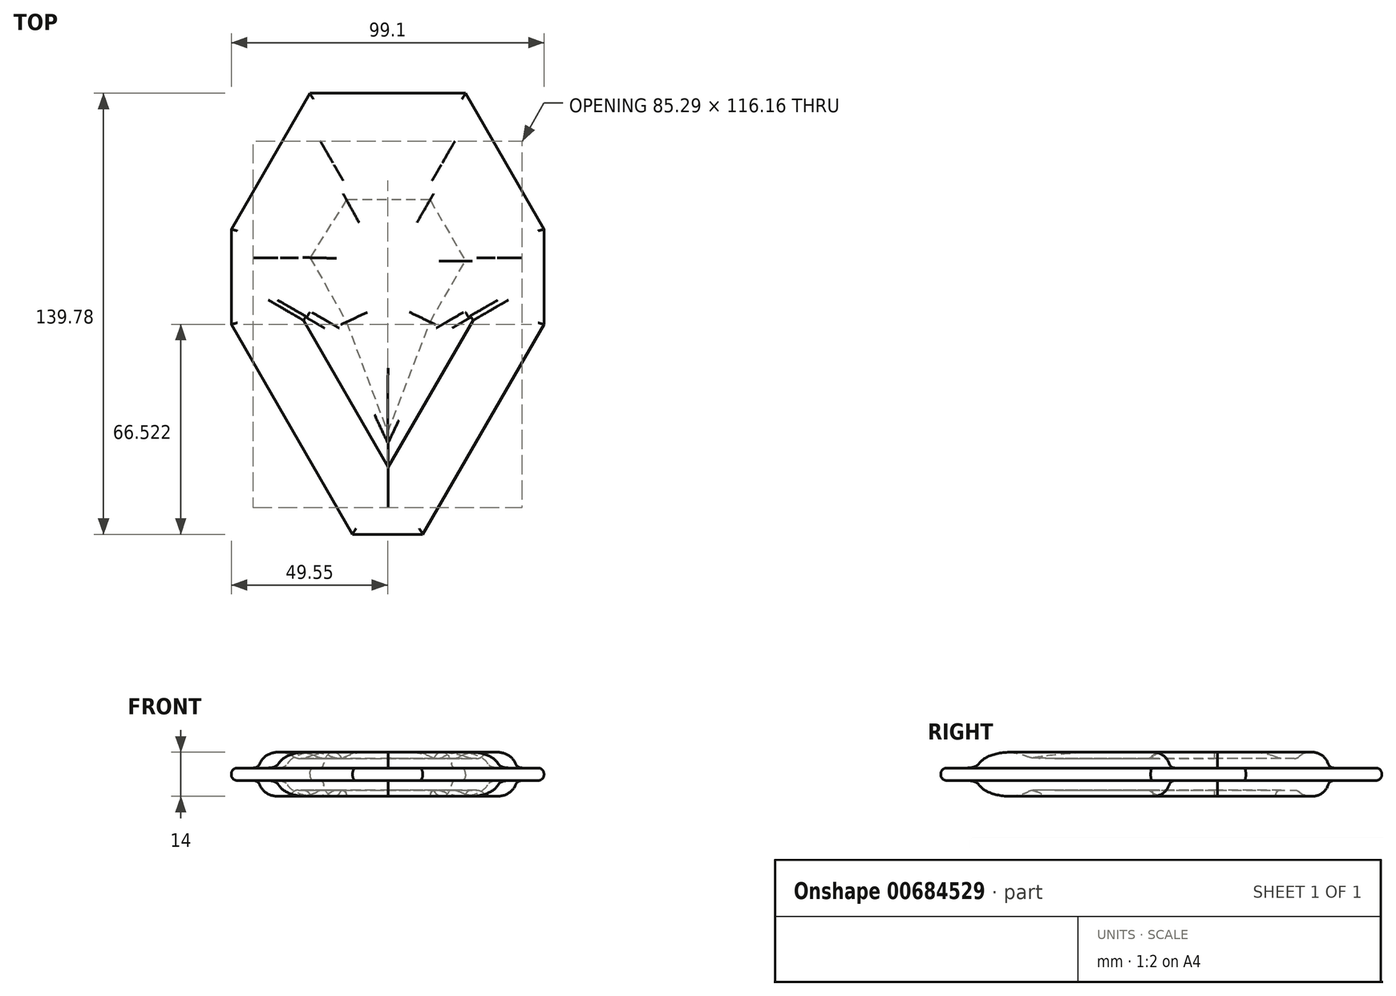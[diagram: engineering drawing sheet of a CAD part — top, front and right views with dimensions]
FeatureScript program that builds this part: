
annotation { "Feature Type Name" : "Feature", "Feature Type Description" : "" }
export const myFeature = defineFeature(function(context is Context, id is Id, definition is map)
    precondition{}
    {
        {
            var Q0;
            Q0=qCreatedBy(makeId("Top.planeOp"),FACE);
            var sketch = newSketch(context, id + "F0", { "sketchPlane" : qUnion([Q0])});
            skCircle(sketch, "E0.cCircle", {"center": v(0, 0) * mm, "radius": 35 * mm, "construction": true});
            skLineSegment(sketch, "E0.0", {"start": v(-20.2, 35) * mm, "end": v(20.2, 35) * mm});
            skLineSegment(sketch, "E0.1", {"start": v(20.2, 35) * mm, "end": v(40.41, 0) * mm});
            skLineSegment(sketch, "E0.2", {"start": v(40.41, 0) * mm, "end": v(31.54, -15.36) * mm});
            skLineSegment(sketch, "E0.4", {"start": v(-31.54, -15.36) * mm, "end": v(-40.41, 0) * mm});
            skLineSegment(sketch, "E0.5", {"start": v(-40.41, 0) * mm, "end": v(-20.2, 35) * mm});
            skPoint(sketch, "E0.0.midPoint", {"position": v(0, 35) * mm});
            skCircle(sketch, "E1.cCircle", {"center": v(0.21, -35.36) * mm, "radius": 20 * mm, "construction": true});
            skLineSegment(sketch, "E1.0", {"start": v(-34.43, -15.36) * mm, "end": v(-31.45, -15.36) * mm});
            skLineSegment(sketch, "E1.1", {"start": v(34.85, -15.36) * mm, "end": v(0.21, -75.36) * mm});
            skLineSegment(sketch, "E1.2", {"start": v(0.21, -75.36) * mm, "end": v(-34.43, -15.36) * mm});
            skPoint(sketch, "E1.0.midPoint", {"position": v(0.21, -15.36) * mm});
            skLineSegment(sketch, "E2.trimOffspring", {"start": v(31.45, -15.36) * mm, "end": v(34.85, -15.36) * mm});
            skPoint(sketch, "E3.orphan", {"position": v(20.2, -35) * mm});
            skPoint(sketch, "E0.3.end.orphan", {"position": v(-19.79, -35.73) * mm});
            skLineSegment(sketch, "E4.0", {"start": v(30.48, 0) * mm, "end": v(18.73, -20.36) * mm});
            skLineSegment(sketch, "E4.1", {"start": v(-18.73, -20.36) * mm, "end": v(-30.48, 0) * mm});
            skLineSegment(sketch, "E4.2", {"start": v(-30.48, 0) * mm, "end": v(-15.24, 26.4) * mm});
            skLineSegment(sketch, "E4.3", {"start": v(-15.24, 26.4) * mm, "end": v(15.24, 26.4) * mm});
            skLineSegment(sketch, "E4.4", {"start": v(15.24, 26.4) * mm, "end": v(30.48, 0) * mm});
            skLineSegment(sketch, "E5.0", {"start": v(0.21, -61.16) * mm, "end": v(-23.35, -20.36) * mm});
            skLineSegment(sketch, "E5.1", {"start": v(23.77, -20.36) * mm, "end": v(0.21, -61.16) * mm});
            skLineSegment(sketch, "E6.0", {"start": v(-23.35, -20.36) * mm, "end": v(-18.73, -20.36) * mm});
            skLineSegment(sketch, "E7.0", {"start": v(18.73, -20.36) * mm, "end": v(23.77, -20.36) * mm});
            skLineSegment(sketch, "E8", {"start": v(-13.02, -20.36) * mm, "end": v(0, -55.36) * mm});
            skLineSegment(sketch, "E9", {"start": v(0, -55.36) * mm, "end": v(13.44, -20.36) * mm});
            skLineSegment(sketch, "E10", {"start": v(13.44, 18.32) * mm, "end": v(-13.02, 18.32) * mm});
            skLineSegment(sketch, "E11", {"start": v(-13.02, 18.32) * mm, "end": v(-24.6, 0) * mm});
            skLineSegment(sketch, "E12", {"start": v(-24.6, 0) * mm, "end": v(-13.02, -20.36) * mm});
            skPoint(sketch, "E13", {"position": v(-24.6, -10.18) * mm});
            skLineSegment(sketch, "E14", {"start": v(13.44, 18.32) * mm, "end": v(24.6, -1.02) * mm});
            skLineSegment(sketch, "E15", {"start": v(13.44, -20.36) * mm, "end": v(24.6, -1.02) * mm});
            skPoint(sketch, "E15.endSnap0", {"position": v(24.6, -10.18) * mm});
            skLineSegment(sketch, "E16", {"start": v(-24.66, 52.11) * mm, "end": v(24.66, 52.11) * mm});
            skLineSegment(sketch, "E17", {"start": v(24.66, 52.11) * mm, "end": v(49.55, 9.01) * mm});
            skLineSegment(sketch, "E18", {"start": v(49.55, 9.01) * mm, "end": v(49.55, -21.14) * mm});
            skLineSegment(sketch, "E19", {"start": v(49.55, -21.14) * mm, "end": v(11.14, -87.67) * mm});
            skLineSegment(sketch, "E20", {"start": v(11.14, -87.67) * mm, "end": v(-11.14, -87.67) * mm});
            skLineSegment(sketch, "E21", {"start": v(-11.14, -87.67) * mm, "end": v(-49.55, -21.14) * mm});
            skLineSegment(sketch, "E22", {"start": v(-49.55, -21.14) * mm, "end": v(-49.55, 9.01) * mm});
            skLineSegment(sketch, "E23", {"start": v(-49.55, 9.01) * mm, "end": v(-24.66, 52.11) * mm});
            skPoint(sketch, "E24", {"position": v(0, 52.11) * mm});
            skSolve(sketch);
        }
        {
            var Q0;
            Q0=makeQuery(id+"F0.imprint","IMPRINT",FACE,{"disambiguationData":[TD([[makeQuery(id+"F0.imprint","IMPRINT",EDGE,{"derivedFrom":sQuery(id+"F0.wireOp",EDGE,"E4.0")}),-1.0]])]});
            extrude(context, id + "F1", {"entities" : qUnion([Q0]), "endBound" : BoundingType.SYMMETRIC, "depth" : 10 * mm, "offsetDistance" : 25 * mm});
        }
        {
            var Q0;
            Q0=makeQuery(id+"F0.imprint","IMPRINT",FACE,{"disambiguationData":[TD([[makeQuery(id+"F0.imprint","IMPRINT",EDGE,{"derivedFrom":sQuery(id+"F0.wireOp",EDGE,"E8")}),1.0]])]});
            var Q1;
            Q1=makeQuery(id+"F0.imprint","IMPRINT",FACE,{"disambiguationData":[TD([[makeQuery(id+"F0.imprint","IMPRINT",EDGE,{"derivedFrom":sQuery(id+"F0.wireOp",EDGE,"E0.0")}),-1.0]])]});
            extrude(context, id + "F2", {"entities" : qUnion([Q0, Q1]), "operationType" : NewBodyOperationType.ADD, "endBound" : BoundingType.SYMMETRIC, "depth" : 14 * mm, "offsetDistance" : 25 * mm});
        }
        {
            var Q0;
            Q0=makeQuery(id+"F0.imprint","IMPRINT",FACE,{"disambiguationData":[TD([[makeQuery(id+"F0.imprint","IMPRINT",EDGE,{"derivedFrom":sQuery(id+"F0.wireOp",EDGE,"E0.0")}),1.0]])]});
            extrude(context, id + "F3", {"entities" : qUnion([Q0]), "operationType" : NewBodyOperationType.ADD, "endBound" : BoundingType.SYMMETRIC, "depth" : 4 * mm, "offsetDistance" : 25 * mm});
        }
        {
            var Q0;
            Q0=makeQuery(id+"F1.opExtrude","CAP_FACE",FACE,{"disambiguationData":[OSD([sQuery(id+"F0.wireOp",EDGE,"E4.0"),sQuery(id+"F0.wireOp",EDGE,"E4.1"),sQuery(id+"F0.wireOp",EDGE,"E4.2"),sQuery(id+"F0.wireOp",EDGE,"E4.3"),sQuery(id+"F0.wireOp",EDGE,"E4.4"),sQuery(id+"F0.wireOp",EDGE,"E5.0"),sQuery(id+"F0.wireOp",EDGE,"E5.1"),sQuery(id+"F0.wireOp",EDGE,"E6.0"),sQuery(id+"F0.wireOp",EDGE,"E7.0"),sQuery(id+"F0.wireOp",EDGE,"E8"),sQuery(id+"F0.wireOp",EDGE,"E9"),sQuery(id+"F0.wireOp",EDGE,"E10"),sQuery(id+"F0.wireOp",EDGE,"E11"),sQuery(id+"F0.wireOp",EDGE,"E12"),sQuery(id+"F0.wireOp",EDGE,"E14"),sQuery(id+"F0.wireOp",EDGE,"E15")])],"isStart":false});
            var Q1;
            Q1=makeQuery(id+"F3.opExtrude","CAP_FACE",FACE,{"disambiguationData":[OSD([sQuery(id+"F0.wireOp",EDGE,"E0.0"),sQuery(id+"F0.wireOp",EDGE,"E0.1"),sQuery(id+"F0.wireOp",EDGE,"E0.2"),sQuery(id+"F0.wireOp",EDGE,"E0.4"),sQuery(id+"F0.wireOp",EDGE,"E0.5"),sQuery(id+"F0.wireOp",EDGE,"E1.0"),sQuery(id+"F0.wireOp",EDGE,"E1.1"),sQuery(id+"F0.wireOp",EDGE,"E1.2"),sQuery(id+"F0.wireOp",EDGE,"E2.trimOffspring"),sQuery(id+"F0.wireOp",EDGE,"E16"),sQuery(id+"F0.wireOp",EDGE,"E17"),sQuery(id+"F0.wireOp",EDGE,"E18"),sQuery(id+"F0.wireOp",EDGE,"E19"),sQuery(id+"F0.wireOp",EDGE,"E20"),sQuery(id+"F0.wireOp",EDGE,"E21"),sQuery(id+"F0.wireOp",EDGE,"E22"),sQuery(id+"F0.wireOp",EDGE,"E23")])],"isStart":false});
            var Q2;
            Q2=makeQuery(id+"F3.opExtrude","CAP_FACE",FACE,{"disambiguationData":[OSD([sQuery(id+"F0.wireOp",EDGE,"E0.0"),sQuery(id+"F0.wireOp",EDGE,"E0.1"),sQuery(id+"F0.wireOp",EDGE,"E0.2"),sQuery(id+"F0.wireOp",EDGE,"E0.4"),sQuery(id+"F0.wireOp",EDGE,"E0.5"),sQuery(id+"F0.wireOp",EDGE,"E1.0"),sQuery(id+"F0.wireOp",EDGE,"E1.1"),sQuery(id+"F0.wireOp",EDGE,"E1.2"),sQuery(id+"F0.wireOp",EDGE,"E2.trimOffspring"),sQuery(id+"F0.wireOp",EDGE,"E16"),sQuery(id+"F0.wireOp",EDGE,"E17"),sQuery(id+"F0.wireOp",EDGE,"E18"),sQuery(id+"F0.wireOp",EDGE,"E19"),sQuery(id+"F0.wireOp",EDGE,"E20"),sQuery(id+"F0.wireOp",EDGE,"E21"),sQuery(id+"F0.wireOp",EDGE,"E22"),sQuery(id+"F0.wireOp",EDGE,"E23")])],"isStart":true});
            var Q3;
            Q3=makeQuery(id+"F1.opExtrude","CAP_FACE",FACE,{"disambiguationData":[OSD([sQuery(id+"F0.wireOp",EDGE,"E4.0"),sQuery(id+"F0.wireOp",EDGE,"E4.1"),sQuery(id+"F0.wireOp",EDGE,"E4.2"),sQuery(id+"F0.wireOp",EDGE,"E4.3"),sQuery(id+"F0.wireOp",EDGE,"E4.4"),sQuery(id+"F0.wireOp",EDGE,"E5.0"),sQuery(id+"F0.wireOp",EDGE,"E5.1"),sQuery(id+"F0.wireOp",EDGE,"E6.0"),sQuery(id+"F0.wireOp",EDGE,"E7.0"),sQuery(id+"F0.wireOp",EDGE,"E8"),sQuery(id+"F0.wireOp",EDGE,"E9"),sQuery(id+"F0.wireOp",EDGE,"E10"),sQuery(id+"F0.wireOp",EDGE,"E11"),sQuery(id+"F0.wireOp",EDGE,"E12"),sQuery(id+"F0.wireOp",EDGE,"E14"),sQuery(id+"F0.wireOp",EDGE,"E15")])],"isStart":true});
            fillet(context, id + "F4", {"entities" : qUnion([Q0, Q1, Q2, Q3]), "radius" : 1.93 * mm, "tangentPropagation" : true, "allowEdgeOverflow" : false});
        }
        {
            var Q0;
            Q0=makeQuery(id+"F2.opExtrude","CAP_FACE",FACE,{"disambiguationData":[OSD([sQuery(id+"F0.wireOp",EDGE,"E0.0"),sQuery(id+"F0.wireOp",EDGE,"E0.1"),sQuery(id+"F0.wireOp",EDGE,"E0.2"),sQuery(id+"F0.wireOp",EDGE,"E0.4"),sQuery(id+"F0.wireOp",EDGE,"E0.5"),sQuery(id+"F0.wireOp",EDGE,"E1.0"),sQuery(id+"F0.wireOp",EDGE,"E1.1"),sQuery(id+"F0.wireOp",EDGE,"E1.2"),sQuery(id+"F0.wireOp",EDGE,"E2.trimOffspring"),sQuery(id+"F0.wireOp",EDGE,"E4.0"),sQuery(id+"F0.wireOp",EDGE,"E4.1"),sQuery(id+"F0.wireOp",EDGE,"E4.2"),sQuery(id+"F0.wireOp",EDGE,"E4.3"),sQuery(id+"F0.wireOp",EDGE,"E4.4"),sQuery(id+"F0.wireOp",EDGE,"E5.0"),sQuery(id+"F0.wireOp",EDGE,"E5.1"),sQuery(id+"F0.wireOp",EDGE,"E6.0"),sQuery(id+"F0.wireOp",EDGE,"E7.0")])],"isStart":false});
            fillet(context, id + "F5", {"entities" : qUnion([Q0]), "radius" : 5.3 * mm, "tangentPropagation" : true, "allowEdgeOverflow" : false});
        }
        {
            var Q0;
            Q0=makeQuery(id+"F2.opExtrude","CAP_FACE",FACE,{"disambiguationData":[OSD([sQuery(id+"F0.wireOp",EDGE,"E8"),sQuery(id+"F0.wireOp",EDGE,"E9"),sQuery(id+"F0.wireOp",EDGE,"E10"),sQuery(id+"F0.wireOp",EDGE,"E11"),sQuery(id+"F0.wireOp",EDGE,"E12"),sQuery(id+"F0.wireOp",EDGE,"E14"),sQuery(id+"F0.wireOp",EDGE,"E15")])],"isStart":false});
            fillet(context, id + "F6", {"entities" : qUnion([Q0]), "radius" : 20 * mm, "tangentPropagation" : true, "allowEdgeOverflow" : false});
        }
        {
            var Q0;
            Q0=makeQuery(id+"F2.opExtrude","CAP_FACE",FACE,{"disambiguationData":[OSD([sQuery(id+"F0.wireOp",EDGE,"E0.0"),sQuery(id+"F0.wireOp",EDGE,"E0.1"),sQuery(id+"F0.wireOp",EDGE,"E0.2"),sQuery(id+"F0.wireOp",EDGE,"E0.4"),sQuery(id+"F0.wireOp",EDGE,"E0.5"),sQuery(id+"F0.wireOp",EDGE,"E1.0"),sQuery(id+"F0.wireOp",EDGE,"E1.1"),sQuery(id+"F0.wireOp",EDGE,"E1.2"),sQuery(id+"F0.wireOp",EDGE,"E2.trimOffspring"),sQuery(id+"F0.wireOp",EDGE,"E4.0"),sQuery(id+"F0.wireOp",EDGE,"E4.1"),sQuery(id+"F0.wireOp",EDGE,"E4.2"),sQuery(id+"F0.wireOp",EDGE,"E4.3"),sQuery(id+"F0.wireOp",EDGE,"E4.4"),sQuery(id+"F0.wireOp",EDGE,"E5.0"),sQuery(id+"F0.wireOp",EDGE,"E5.1"),sQuery(id+"F0.wireOp",EDGE,"E6.0"),sQuery(id+"F0.wireOp",EDGE,"E7.0")])],"isStart":true});
            fillet(context, id + "F7", {"entities" : qUnion([Q0]), "radius" : 5.3 * mm, "tangentPropagation" : true, "allowEdgeOverflow" : false});
        }
    });
